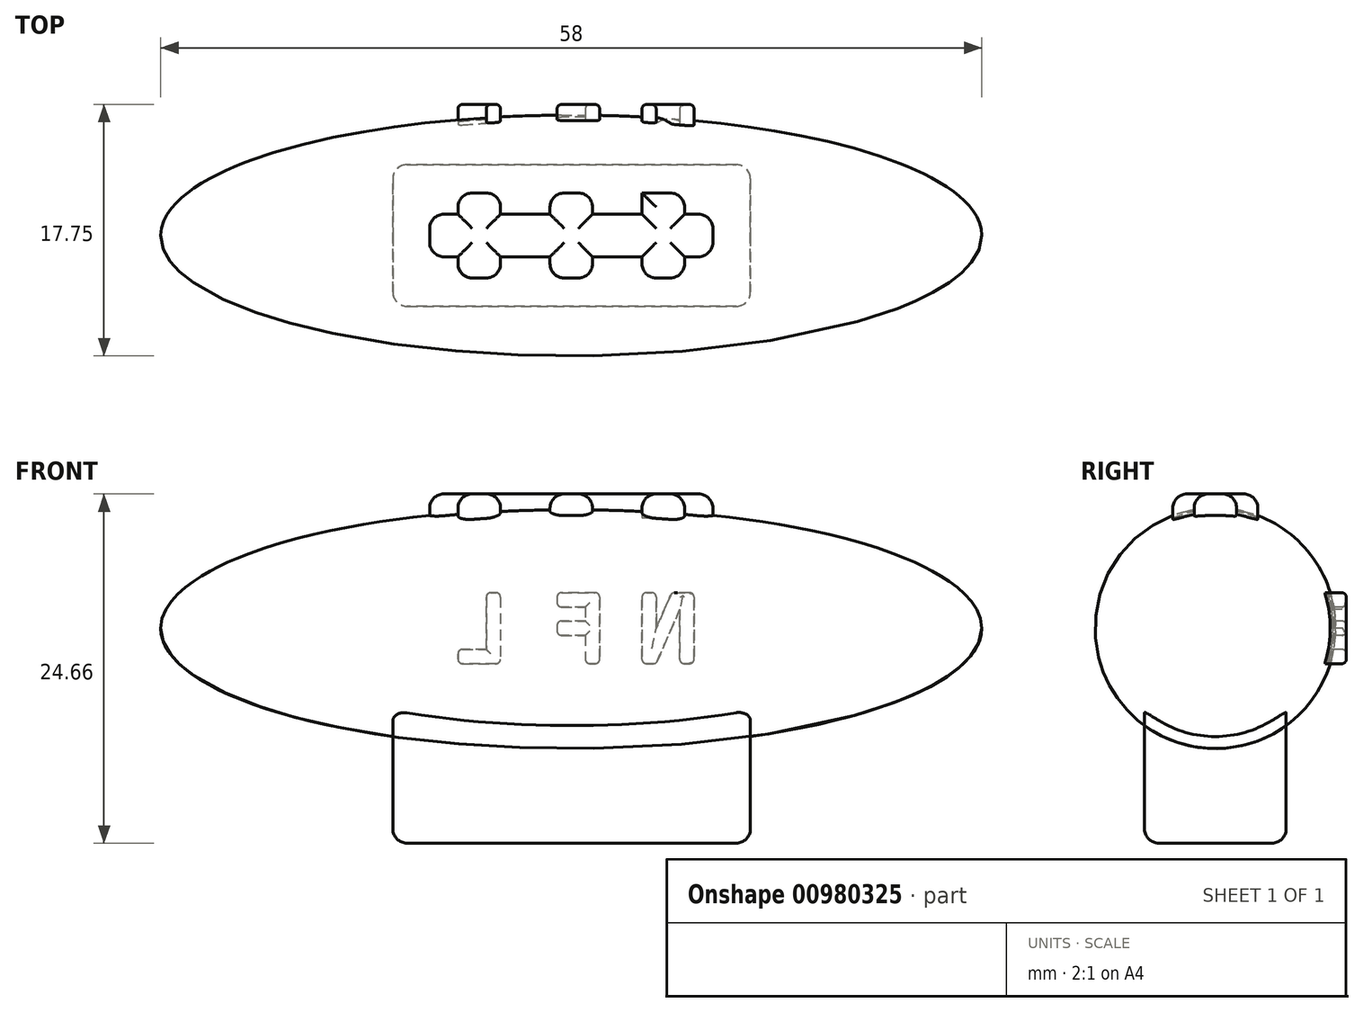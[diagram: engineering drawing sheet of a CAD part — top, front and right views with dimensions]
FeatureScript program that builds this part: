
annotation { "Feature Type Name" : "Feature", "Feature Type Description" : "" }
export const myFeature = defineFeature(function(context is Context, id is Id, definition is map)
    precondition{}
    {
        {
            var Q0;
            Q0=qCreatedBy(makeId("Front.planeOp"),FACE);
            var sketch = newSketch(context, id + "F0", { "sketchPlane" : qUnion([Q0])});
            skEllipse(sketch, "E0", {"center": v(0, 0) * mm, "majorRadius": 29 * mm, "minorRadius": 8.5 * mm, "majorAxis": v(-1, 0)});
            skLineSegment(sketch, "E1", {"start": v(-35.24, 0) * mm, "end": v(46.74, 0) * mm});
            skSolve(sketch);
        }
        {
            var Q0;
            {var subQ0=sQuery(id+"F0.wireOp",EDGE,"E1");var subQ1=sQuery(id+"F0.wireOp",EDGE,"E0");var subQ2=makeQuery(id+"F0.imprint","INTERSECT",VERTEX,{"disambiguationData":[OD(0.0)],"derivedFrom":[subQ1,subQ0]});Q0=makeQuery(id+"F0.imprint","IMPRINT",FACE,{"disambiguationData":[TD([[makeQuery(id+"F0.imprint","IMPRINT",EDGE,{"disambiguationData":[TD([[subQ2,1.0]])],"derivedFrom":subQ1}),1.0]])]});}
            var Q1;
            Q1=sQuery(id+"F0.wireOp",EDGE,"E1");
            revolve(context, id + "F1", {"surfaceOperationType" : NewSurfaceOperationType.NEW, "entities" : qUnion([Q0]), "axis" : qUnion([Q1]), "revolveType" : RevolveType.FULL});
        }
        {
            var Q0;
            Q0=qCreatedBy(makeId("Front.planeOp"),FACE);
            var sketch = newSketch(context, id + "F2", { "sketchPlane" : qUnion([Q0])});
            skLineSegment(sketch, "E2", {"start": v(-10, 7.5) * mm, "end": v(-10, 9.48) * mm});
            skLineSegment(sketch, "E3", {"start": v(-10, 9.48) * mm, "end": v(10, 9.48) * mm});
            skLineSegment(sketch, "E4", {"start": v(10, 9.48) * mm, "end": v(10, 7.5) * mm});
            skLineSegment(sketch, "E5", {"start": v(-10, 7.5) * mm, "end": v(10, 7.5) * mm});
            skSolve(sketch);
        }
        {
            var Q0;
            Q0 = qSketchRegion(id + "F2", true);
            extrude(context, id + "F3", {"entities" : qUnion([Q0]), "operationType" : NewBodyOperationType.ADD, "depth" : 3 * mm, "offsetDistance" : 25 * mm, "symmetric" : true});
        }
        {
            var Q0;
            Q0=qCreatedBy(makeId("Front.planeOp"),FACE);
            var sketch = newSketch(context, id + "F4", { "sketchPlane" : qUnion([Q0])});
            skLineSegment(sketch, "E6", {"start": v(-8, 9.48) * mm, "end": v(-8, 7.35) * mm});
            skLineSegment(sketch, "E7", {"start": v(-8, 7.35) * mm, "end": v(-5, 7.35) * mm});
            skLineSegment(sketch, "E8", {"start": v(-5, 7.35) * mm, "end": v(-5, 9.48) * mm});
            skLineSegment(sketch, "E9", {"start": v(-5, 9.48) * mm, "end": v(-8, 9.48) * mm});
            skLineSegment(sketch, "E10", {"start": v(-1.5, 9.48) * mm, "end": v(-1.5, 7.25) * mm});
            skLineSegment(sketch, "E11", {"start": v(-1.5, 7.25) * mm, "end": v(1.5, 7.25) * mm});
            skLineSegment(sketch, "E12", {"start": v(1.5, 7.25) * mm, "end": v(1.5, 9.48) * mm});
            skLineSegment(sketch, "E13", {"start": v(1.5, 9.48) * mm, "end": v(-1.5, 9.48) * mm});
            skLineSegment(sketch, "E14", {"start": v(5, 9.48) * mm, "end": v(5, 7.11) * mm});
            skLineSegment(sketch, "E15", {"start": v(5, 7.11) * mm, "end": v(8, 7.11) * mm});
            skLineSegment(sketch, "E16", {"start": v(8, 7.11) * mm, "end": v(8, 9.48) * mm});
            skLineSegment(sketch, "E17", {"start": v(8, 9.48) * mm, "end": v(5, 9.48) * mm});
            skSolve(sketch);
        }
        {
            var Q0;
            Q0=makeQuery(id+"F4.imprint","IMPRINT",FACE,{"disambiguationData":[TD([[makeQuery(id+"F4.imprint","IMPRINT",EDGE,{"derivedFrom":sQuery(id+"F4.wireOp",EDGE,"E6")}),1.0]])]});
            var Q1;
            Q1=makeQuery(id+"F4.imprint","IMPRINT",FACE,{"disambiguationData":[TD([[makeQuery(id+"F4.imprint","IMPRINT",EDGE,{"derivedFrom":sQuery(id+"F4.wireOp",EDGE,"E10")}),1.0]])]});
            var Q2;
            Q2=makeQuery(id+"F4.imprint","IMPRINT",FACE,{"disambiguationData":[TD([[makeQuery(id+"F4.imprint","IMPRINT",EDGE,{"derivedFrom":sQuery(id+"F4.wireOp",EDGE,"E14")}),1.0]])]});
            extrude(context, id + "F5", {"entities" : qUnion([Q0, Q1, Q2]), "operationType" : NewBodyOperationType.ADD, "depth" : 6 * mm, "offsetDistance" : 25 * mm, "symmetric" : true});
        }
        {
            var Q0;
            Q0=qCreatedBy(makeId("Front.planeOp"),FACE);
            var sketch = newSketch(context, id + "F6", { "sketchPlane" : qUnion([Q0])});
            skLineSegment(sketch, "E18", {"start": v(12.65, -5.45) * mm, "end": v(-12.6, -5.45) * mm});
            skLineSegment(sketch, "E19", {"start": v(-12.6, -5.45) * mm, "end": v(-12.6, -15.18) * mm});
            skLineSegment(sketch, "E20", {"start": v(-12.6, -15.18) * mm, "end": v(12.65, -15.18) * mm});
            skLineSegment(sketch, "E21", {"start": v(12.65, -5.45) * mm, "end": v(12.65, -15.18) * mm});
            skSolve(sketch);
        }
        {
            var Q0;
            Q0=makeQuery(id+"F6.imprint","IMPRINT",FACE,{"disambiguationData":[TD([[makeQuery(id+"F6.imprint","IMPRINT",EDGE,{"derivedFrom":sQuery(id+"F6.wireOp",EDGE,"E18")}),1.0]])]});
            extrude(context, id + "F7", {"entities" : qUnion([Q0]), "operationType" : NewBodyOperationType.ADD, "depth" : 10 * mm, "offsetDistance" : 25 * mm, "symmetric" : true});
        }
        {
            var Q0;
            Q0=qCreatedBy(makeId("Front.planeOp"),FACE);
            cPlane(context, id + "F8", {"entities" : qUnion([Q0]), "cplaneType" : CPlaneType.OFFSET, "offset" : 8.5 * mm, "oppositeDirection" : true, "width" : 150 * mm, "height" : 150 * mm});
        }
        {
            var Q0;
            Q0=qCreatedBy(id+"F8.planeOp",FACE);
            var sketch = newSketch(context, id + "F9", { "sketchPlane" : qUnion([Q0])});
            skLineSegment(sketch, "E22", {"start": v(8.67, -2.5) * mm, "end": v(8.67, 2.5) * mm});
            skLineSegment(sketch, "E23", {"start": v(8.67, 2.5) * mm, "end": v(7.1, 2.5) * mm});
            skLineSegment(sketch, "E24", {"start": v(7.1, 2.5) * mm, "end": v(6, 0) * mm});
            skLineSegment(sketch, "E25", {"start": v(6, 0) * mm, "end": v(6, 2.5) * mm});
            skLineSegment(sketch, "E26", {"start": v(8.67, -2.5) * mm, "end": v(7.67, -2.5) * mm});
            skLineSegment(sketch, "E27", {"start": v(7.67, -2.5) * mm, "end": v(7.67, 1.33) * mm});
            skLineSegment(sketch, "E28", {"start": v(5, 2.5) * mm, "end": v(6, 2.5) * mm});
            skLineSegment(sketch, "E29", {"start": v(7.67, 1.33) * mm, "end": v(6, -2.5) * mm});
            skLineSegment(sketch, "E30", {"start": v(6, -2.5) * mm, "end": v(5, -2.5) * mm});
            skLineSegment(sketch, "E31", {"start": v(5, -2.5) * mm, "end": v(5, 2.5) * mm});
            skLineSegment(sketch, "E32", {"start": v(2, -2.5) * mm, "end": v(2, 2.5) * mm});
            skLineSegment(sketch, "E33", {"start": v(2, 2.5) * mm, "end": v(-1, 2.5) * mm});
            skLineSegment(sketch, "E34", {"start": v(-1, 2.5) * mm, "end": v(-1, 1.5) * mm});
            skLineSegment(sketch, "E35", {"start": v(-1, 1.5) * mm, "end": v(1, 1.5) * mm});
            skLineSegment(sketch, "E36", {"start": v(1, 1.5) * mm, "end": v(1, 0.5) * mm});
            skLineSegment(sketch, "E37", {"start": v(1, 0.5) * mm, "end": v(-1, 0.5) * mm});
            skLineSegment(sketch, "E38", {"start": v(-1, 0.5) * mm, "end": v(-1, -0.5) * mm});
            skLineSegment(sketch, "E39", {"start": v(-1, -0.5) * mm, "end": v(1, -0.5) * mm});
            skLineSegment(sketch, "E40", {"start": v(1, -0.5) * mm, "end": v(1, -2.5) * mm});
            skLineSegment(sketch, "E41", {"start": v(1, -2.5) * mm, "end": v(2, -2.5) * mm});
            skLineSegment(sketch, "E42", {"start": v(-5, 2.5) * mm, "end": v(-5, -2.5) * mm});
            skLineSegment(sketch, "E43", {"start": v(-5, -2.5) * mm, "end": v(-8, -2.5) * mm});
            skLineSegment(sketch, "E44", {"start": v(-8, -2.5) * mm, "end": v(-8, -1.5) * mm});
            skLineSegment(sketch, "E45", {"start": v(-8, -1.5) * mm, "end": v(-6, -1.5) * mm});
            skLineSegment(sketch, "E46", {"start": v(-6, -1.5) * mm, "end": v(-6, 2.5) * mm});
            skLineSegment(sketch, "E47", {"start": v(-6, 2.5) * mm, "end": v(-5, 2.5) * mm});
            skSolve(sketch);
        }
        {
            var Q0;
            Q0=makeQuery(id+"F9.imprint","IMPRINT",FACE,{"disambiguationData":[TD([[makeQuery(id+"F9.imprint","IMPRINT",EDGE,{"derivedFrom":sQuery(id+"F9.wireOp",EDGE,"E22")}),1.0]])]});
            var Q1;
            Q1=makeQuery(id+"F9.imprint","IMPRINT",FACE,{"disambiguationData":[TD([[makeQuery(id+"F9.imprint","IMPRINT",EDGE,{"derivedFrom":sQuery(id+"F9.wireOp",EDGE,"E32")}),1.0]])]});
            var Q2;
            Q2=makeQuery(id+"F9.imprint","IMPRINT",FACE,{"disambiguationData":[TD([[makeQuery(id+"F9.imprint","IMPRINT",EDGE,{"derivedFrom":sQuery(id+"F9.wireOp",EDGE,"E42")}),-1.0]])]});
            extrude(context, id + "F10", {"entities" : qUnion([Q0, Q1, Q2]), "operationType" : NewBodyOperationType.ADD, "oppositeDirection" : true, "depth" : 1.5 * mm, "offsetDistance" : 25 * mm, "symmetric" : true});
        }
        {
            var Q0;
            Q0=makeQuery(id+"F5.opExtrude","CAP_EDGE",EDGE,{"disambiguationData":[OSD([sQuery(id+"F4.wireOp",EDGE,"E17")])],"isStart":false});
            var Q1;
            {var subQ0=sQuery(id+"F4.wireOp",EDGE,"E16");var subQ1=sQuery(id+"F2.wireOp",EDGE,"E3");var subQ2=sQuery(id+"F4.wireOp",EDGE,"E17");Q1=makeQuery(id+"F5.boolean.opBoolean","SPLIT",EDGE,{"disambiguationData":[TD([makeQuery(id+"F3.opExtrude","CAP_FACE",FACE,{"disambiguationData":[OSD([sQuery(id+"F2.wireOp",EDGE,"E2"),subQ1,sQuery(id+"F2.wireOp",EDGE,"E4"),sQuery(id+"F2.wireOp",EDGE,"E5")])],"isStart":false})])],"derivedFrom":makeQuery(id+"F5.opExtrude","SWEPT_EDGE",EDGE,{"disambiguationData":[OSD([subQ0,subQ2])]})});}
            var Q2;
            {var subQ0=sQuery(id+"F2.wireOp",EDGE,"E4");var subQ1=sQuery(id+"F2.wireOp",EDGE,"E3");Q2=makeQuery(id+"F5.boolean.opBoolean","SPLIT",EDGE,{"disambiguationData":[TD([makeQuery(id+"F3.opExtrude","SWEPT_FACE",FACE,{"disambiguationData":[OSD([subQ0])]})])],"derivedFrom":makeQuery(id+"F3.opExtrude","CAP_EDGE",EDGE,{"disambiguationData":[OSD([subQ1])],"isStart":false})});}
            var Q3;
            Q3=makeQuery(id+"F3.opExtrude","SWEPT_EDGE",EDGE,{"disambiguationData":[OSD([sQuery(id+"F2.wireOp",EDGE,"E3"),sQuery(id+"F2.wireOp",EDGE,"E4")])]});
            var Q4;
            {var subQ0=sQuery(id+"F2.wireOp",EDGE,"E4");var subQ1=sQuery(id+"F2.wireOp",EDGE,"E3");Q4=makeQuery(id+"F5.boolean.opBoolean","SPLIT",EDGE,{"disambiguationData":[TD([makeQuery(id+"F3.opExtrude","SWEPT_FACE",FACE,{"disambiguationData":[OSD([subQ0])]})])],"derivedFrom":makeQuery(id+"F3.opExtrude","CAP_EDGE",EDGE,{"disambiguationData":[OSD([subQ1])],"isStart":true})});}
            var Q5;
            {var subQ0=sQuery(id+"F4.wireOp",EDGE,"E16");var subQ1=sQuery(id+"F2.wireOp",EDGE,"E3");var subQ2=sQuery(id+"F4.wireOp",EDGE,"E17");Q5=makeQuery(id+"F5.boolean.opBoolean","SPLIT",EDGE,{"disambiguationData":[TD([makeQuery(id+"F3.opExtrude","CAP_FACE",FACE,{"disambiguationData":[OSD([sQuery(id+"F2.wireOp",EDGE,"E2"),subQ1,sQuery(id+"F2.wireOp",EDGE,"E4"),sQuery(id+"F2.wireOp",EDGE,"E5")])],"isStart":true})])],"derivedFrom":makeQuery(id+"F5.opExtrude","SWEPT_EDGE",EDGE,{"disambiguationData":[OSD([subQ0,subQ2])]})});}
            var Q6;
            {var subQ0=sQuery(id+"F2.wireOp",EDGE,"E3");Q6=makeQuery(id+"F5.boolean.opBoolean","SPLIT",EDGE,{"disambiguationData":[TD([makeQuery(id+"F5.opExtrude","SWEPT_FACE",FACE,{"disambiguationData":[OSD([sQuery(id+"F4.wireOp",EDGE,"E12")])]})])],"derivedFrom":makeQuery(id+"F3.opExtrude","CAP_EDGE",EDGE,{"disambiguationData":[OSD([subQ0])],"isStart":true})});}
            var Q7;
            {var subQ0=sQuery(id+"F2.wireOp",EDGE,"E3");var subQ1=sQuery(id+"F4.wireOp",EDGE,"E14");var subQ2=sQuery(id+"F4.wireOp",EDGE,"E17");Q7=makeQuery(id+"F5.boolean.opBoolean","SPLIT",EDGE,{"disambiguationData":[TD([makeQuery(id+"F3.opExtrude","CAP_FACE",FACE,{"disambiguationData":[OSD([sQuery(id+"F2.wireOp",EDGE,"E2"),subQ0,sQuery(id+"F2.wireOp",EDGE,"E4"),sQuery(id+"F2.wireOp",EDGE,"E5")])],"isStart":false})])],"derivedFrom":makeQuery(id+"F5.opExtrude","SWEPT_EDGE",EDGE,{"disambiguationData":[OSD([subQ1,subQ2])]})});}
            var Q8;
            Q8=makeQuery(id+"F5.opExtrude","CAP_EDGE",EDGE,{"disambiguationData":[OSD([sQuery(id+"F4.wireOp",EDGE,"E17")])],"isStart":true});
            var Q9;
            {var subQ0=sQuery(id+"F2.wireOp",EDGE,"E3");var subQ1=sQuery(id+"F4.wireOp",EDGE,"E14");var subQ2=sQuery(id+"F4.wireOp",EDGE,"E17");Q9=makeQuery(id+"F5.boolean.opBoolean","SPLIT",EDGE,{"disambiguationData":[TD([makeQuery(id+"F3.opExtrude","CAP_FACE",FACE,{"disambiguationData":[OSD([sQuery(id+"F2.wireOp",EDGE,"E2"),subQ0,sQuery(id+"F2.wireOp",EDGE,"E4"),sQuery(id+"F2.wireOp",EDGE,"E5")])],"isStart":true})])],"derivedFrom":makeQuery(id+"F5.opExtrude","SWEPT_EDGE",EDGE,{"disambiguationData":[OSD([subQ1,subQ2])]})});}
            var Q10;
            {var subQ0=sQuery(id+"F2.wireOp",EDGE,"E3");Q10=makeQuery(id+"F5.boolean.opBoolean","SPLIT",EDGE,{"disambiguationData":[TD([makeQuery(id+"F5.opExtrude","SWEPT_FACE",FACE,{"disambiguationData":[OSD([sQuery(id+"F4.wireOp",EDGE,"E12")])]})])],"derivedFrom":makeQuery(id+"F3.opExtrude","CAP_EDGE",EDGE,{"disambiguationData":[OSD([subQ0])],"isStart":false})});}
            var Q11;
            {var subQ0=sQuery(id+"F2.wireOp",EDGE,"E3");var subQ1=sQuery(id+"F4.wireOp",EDGE,"E13");var subQ2=sQuery(id+"F4.wireOp",EDGE,"E12");Q11=makeQuery(id+"F5.boolean.opBoolean","SPLIT",EDGE,{"disambiguationData":[TD([makeQuery(id+"F3.opExtrude","CAP_FACE",FACE,{"disambiguationData":[OSD([sQuery(id+"F2.wireOp",EDGE,"E2"),subQ0,sQuery(id+"F2.wireOp",EDGE,"E4"),sQuery(id+"F2.wireOp",EDGE,"E5")])],"isStart":false})])],"derivedFrom":makeQuery(id+"F5.opExtrude","SWEPT_EDGE",EDGE,{"disambiguationData":[OSD([subQ2,subQ1])]})});}
            var Q12;
            Q12=makeQuery(id+"F5.opExtrude","CAP_EDGE",EDGE,{"disambiguationData":[OSD([sQuery(id+"F4.wireOp",EDGE,"E13")])],"isStart":false});
            var Q13;
            {var subQ0=sQuery(id+"F4.wireOp",EDGE,"E10");var subQ1=sQuery(id+"F2.wireOp",EDGE,"E3");var subQ2=sQuery(id+"F4.wireOp",EDGE,"E13");Q13=makeQuery(id+"F5.boolean.opBoolean","SPLIT",EDGE,{"disambiguationData":[TD([makeQuery(id+"F3.opExtrude","CAP_FACE",FACE,{"disambiguationData":[OSD([sQuery(id+"F2.wireOp",EDGE,"E2"),subQ1,sQuery(id+"F2.wireOp",EDGE,"E4"),sQuery(id+"F2.wireOp",EDGE,"E5")])],"isStart":false})])],"derivedFrom":makeQuery(id+"F5.opExtrude","SWEPT_EDGE",EDGE,{"disambiguationData":[OSD([subQ0,subQ2])]})});}
            var Q14;
            {var subQ0=sQuery(id+"F2.wireOp",EDGE,"E3");Q14=makeQuery(id+"F5.boolean.opBoolean","SPLIT",EDGE,{"disambiguationData":[TD([makeQuery(id+"F5.opExtrude","SWEPT_FACE",FACE,{"disambiguationData":[OSD([sQuery(id+"F4.wireOp",EDGE,"E8")])]})])],"derivedFrom":makeQuery(id+"F3.opExtrude","CAP_EDGE",EDGE,{"disambiguationData":[OSD([subQ0])],"isStart":false})});}
            var Q15;
            {var subQ0=sQuery(id+"F4.wireOp",EDGE,"E9");var subQ1=sQuery(id+"F4.wireOp",EDGE,"E8");var subQ2=sQuery(id+"F2.wireOp",EDGE,"E3");Q15=makeQuery(id+"F5.boolean.opBoolean","SPLIT",EDGE,{"disambiguationData":[TD([makeQuery(id+"F3.opExtrude","CAP_FACE",FACE,{"disambiguationData":[OSD([sQuery(id+"F2.wireOp",EDGE,"E2"),subQ2,sQuery(id+"F2.wireOp",EDGE,"E4"),sQuery(id+"F2.wireOp",EDGE,"E5")])],"isStart":false})])],"derivedFrom":makeQuery(id+"F5.opExtrude","SWEPT_EDGE",EDGE,{"disambiguationData":[OSD([subQ1,subQ0])]})});}
            var Q16;
            Q16=makeQuery(id+"F5.opExtrude","CAP_EDGE",EDGE,{"disambiguationData":[OSD([sQuery(id+"F4.wireOp",EDGE,"E9")])],"isStart":false});
            var Q17;
            {var subQ0=sQuery(id+"F4.wireOp",EDGE,"E9");var subQ1=sQuery(id+"F4.wireOp",EDGE,"E6");var subQ2=sQuery(id+"F2.wireOp",EDGE,"E3");Q17=makeQuery(id+"F5.boolean.opBoolean","SPLIT",EDGE,{"disambiguationData":[TD([makeQuery(id+"F3.opExtrude","CAP_FACE",FACE,{"disambiguationData":[OSD([sQuery(id+"F2.wireOp",EDGE,"E2"),subQ2,sQuery(id+"F2.wireOp",EDGE,"E4"),sQuery(id+"F2.wireOp",EDGE,"E5")])],"isStart":false})])],"derivedFrom":makeQuery(id+"F5.opExtrude","SWEPT_EDGE",EDGE,{"disambiguationData":[OSD([subQ1,subQ0])]})});}
            var Q18;
            {var subQ0=sQuery(id+"F2.wireOp",EDGE,"E3");var subQ1=sQuery(id+"F2.wireOp",EDGE,"E2");Q18=makeQuery(id+"F5.boolean.opBoolean","SPLIT",EDGE,{"disambiguationData":[TD([makeQuery(id+"F3.opExtrude","SWEPT_FACE",FACE,{"disambiguationData":[OSD([subQ1])]})])],"derivedFrom":makeQuery(id+"F3.opExtrude","CAP_EDGE",EDGE,{"disambiguationData":[OSD([subQ0])],"isStart":false})});}
            var Q19;
            Q19=makeQuery(id+"F3.opExtrude","SWEPT_EDGE",EDGE,{"disambiguationData":[OSD([sQuery(id+"F2.wireOp",EDGE,"E2"),sQuery(id+"F2.wireOp",EDGE,"E3")])]});
            var Q20;
            {var subQ0=sQuery(id+"F2.wireOp",EDGE,"E3");var subQ1=sQuery(id+"F4.wireOp",EDGE,"E13");var subQ2=sQuery(id+"F4.wireOp",EDGE,"E12");Q20=makeQuery(id+"F5.boolean.opBoolean","SPLIT",EDGE,{"disambiguationData":[TD([makeQuery(id+"F3.opExtrude","CAP_FACE",FACE,{"disambiguationData":[OSD([sQuery(id+"F2.wireOp",EDGE,"E2"),subQ0,sQuery(id+"F2.wireOp",EDGE,"E4"),sQuery(id+"F2.wireOp",EDGE,"E5")])],"isStart":true})])],"derivedFrom":makeQuery(id+"F5.opExtrude","SWEPT_EDGE",EDGE,{"disambiguationData":[OSD([subQ2,subQ1])]})});}
            var Q21;
            Q21=makeQuery(id+"F5.opExtrude","CAP_EDGE",EDGE,{"disambiguationData":[OSD([sQuery(id+"F4.wireOp",EDGE,"E9")])],"isStart":true});
            var Q22;
            {var subQ0=sQuery(id+"F2.wireOp",EDGE,"E3");Q22=makeQuery(id+"F5.boolean.opBoolean","SPLIT",EDGE,{"disambiguationData":[TD([makeQuery(id+"F5.opExtrude","SWEPT_FACE",FACE,{"disambiguationData":[OSD([sQuery(id+"F4.wireOp",EDGE,"E8")])]})])],"derivedFrom":makeQuery(id+"F3.opExtrude","CAP_EDGE",EDGE,{"disambiguationData":[OSD([subQ0])],"isStart":true})});}
            var Q23;
            Q23=makeQuery(id+"F5.opExtrude","CAP_EDGE",EDGE,{"disambiguationData":[OSD([sQuery(id+"F4.wireOp",EDGE,"E13")])],"isStart":true});
            var Q24;
            {var subQ0=sQuery(id+"F4.wireOp",EDGE,"E10");var subQ1=sQuery(id+"F2.wireOp",EDGE,"E3");var subQ2=sQuery(id+"F4.wireOp",EDGE,"E13");Q24=makeQuery(id+"F5.boolean.opBoolean","SPLIT",EDGE,{"disambiguationData":[TD([makeQuery(id+"F3.opExtrude","CAP_FACE",FACE,{"disambiguationData":[OSD([sQuery(id+"F2.wireOp",EDGE,"E2"),subQ1,sQuery(id+"F2.wireOp",EDGE,"E4"),sQuery(id+"F2.wireOp",EDGE,"E5")])],"isStart":true})])],"derivedFrom":makeQuery(id+"F5.opExtrude","SWEPT_EDGE",EDGE,{"disambiguationData":[OSD([subQ0,subQ2])]})});}
            var Q25;
            {var subQ0=sQuery(id+"F4.wireOp",EDGE,"E9");var subQ1=sQuery(id+"F4.wireOp",EDGE,"E8");var subQ2=sQuery(id+"F2.wireOp",EDGE,"E3");Q25=makeQuery(id+"F5.boolean.opBoolean","SPLIT",EDGE,{"disambiguationData":[TD([makeQuery(id+"F3.opExtrude","CAP_FACE",FACE,{"disambiguationData":[OSD([sQuery(id+"F2.wireOp",EDGE,"E2"),subQ2,sQuery(id+"F2.wireOp",EDGE,"E4"),sQuery(id+"F2.wireOp",EDGE,"E5")])],"isStart":true})])],"derivedFrom":makeQuery(id+"F5.opExtrude","SWEPT_EDGE",EDGE,{"disambiguationData":[OSD([subQ1,subQ0])]})});}
            var Q26;
            {var subQ0=sQuery(id+"F4.wireOp",EDGE,"E9");var subQ1=sQuery(id+"F4.wireOp",EDGE,"E6");var subQ2=sQuery(id+"F2.wireOp",EDGE,"E3");Q26=makeQuery(id+"F5.boolean.opBoolean","SPLIT",EDGE,{"disambiguationData":[TD([makeQuery(id+"F3.opExtrude","CAP_FACE",FACE,{"disambiguationData":[OSD([sQuery(id+"F2.wireOp",EDGE,"E2"),subQ2,sQuery(id+"F2.wireOp",EDGE,"E4"),sQuery(id+"F2.wireOp",EDGE,"E5")])],"isStart":true})])],"derivedFrom":makeQuery(id+"F5.opExtrude","SWEPT_EDGE",EDGE,{"disambiguationData":[OSD([subQ1,subQ0])]})});}
            var Q27;
            {var subQ0=sQuery(id+"F2.wireOp",EDGE,"E3");var subQ1=sQuery(id+"F2.wireOp",EDGE,"E2");Q27=makeQuery(id+"F5.boolean.opBoolean","SPLIT",EDGE,{"disambiguationData":[TD([makeQuery(id+"F3.opExtrude","SWEPT_FACE",FACE,{"disambiguationData":[OSD([subQ1])]})])],"derivedFrom":makeQuery(id+"F3.opExtrude","CAP_EDGE",EDGE,{"disambiguationData":[OSD([subQ0])],"isStart":true})});}
            var Q28;
            Q28=makeQuery(id+"F5.opExtrude","CAP_EDGE",EDGE,{"disambiguationData":[OSD([sQuery(id+"F4.wireOp",EDGE,"E16")])],"isStart":true});
            var Q29;
            Q29=makeQuery(id+"F3.opExtrude","CAP_EDGE",EDGE,{"disambiguationData":[OSD([sQuery(id+"F2.wireOp",EDGE,"E4")])],"isStart":true});
            var Q30;
            Q30=makeQuery(id+"F3.opExtrude","CAP_EDGE",EDGE,{"disambiguationData":[OSD([sQuery(id+"F2.wireOp",EDGE,"E4")])],"isStart":false});
            var Q31;
            Q31=makeQuery(id+"F5.opExtrude","CAP_EDGE",EDGE,{"disambiguationData":[OSD([sQuery(id+"F4.wireOp",EDGE,"E12")])],"isStart":true});
            var Q32;
            Q32=makeQuery(id+"F5.opExtrude","CAP_EDGE",EDGE,{"disambiguationData":[OSD([sQuery(id+"F4.wireOp",EDGE,"E10")])],"isStart":true});
            var Q33;
            Q33=makeQuery(id+"F5.opExtrude","CAP_EDGE",EDGE,{"disambiguationData":[OSD([sQuery(id+"F4.wireOp",EDGE,"E8")])],"isStart":true});
            var Q34;
            Q34=makeQuery(id+"F5.opExtrude","CAP_EDGE",EDGE,{"disambiguationData":[OSD([sQuery(id+"F4.wireOp",EDGE,"E6")])],"isStart":true});
            var Q35;
            Q35=makeQuery(id+"F3.opExtrude","CAP_EDGE",EDGE,{"disambiguationData":[OSD([sQuery(id+"F2.wireOp",EDGE,"E2")])],"isStart":true});
            var Q36;
            Q36=makeQuery(id+"F3.opExtrude","CAP_EDGE",EDGE,{"disambiguationData":[OSD([sQuery(id+"F2.wireOp",EDGE,"E2")])],"isStart":false});
            var Q37;
            Q37=makeQuery(id+"F5.opExtrude","CAP_EDGE",EDGE,{"disambiguationData":[OSD([sQuery(id+"F4.wireOp",EDGE,"E6")])],"isStart":false});
            var Q38;
            Q38=makeQuery(id+"F5.opExtrude","CAP_EDGE",EDGE,{"disambiguationData":[OSD([sQuery(id+"F4.wireOp",EDGE,"E8")])],"isStart":false});
            var Q39;
            Q39=makeQuery(id+"F5.opExtrude","CAP_EDGE",EDGE,{"disambiguationData":[OSD([sQuery(id+"F4.wireOp",EDGE,"E10")])],"isStart":false});
            var Q40;
            Q40=makeQuery(id+"F5.opExtrude","CAP_EDGE",EDGE,{"disambiguationData":[OSD([sQuery(id+"F4.wireOp",EDGE,"E12")])],"isStart":false});
            var Q41;
            Q41=makeQuery(id+"F5.opExtrude","CAP_EDGE",EDGE,{"disambiguationData":[OSD([sQuery(id+"F4.wireOp",EDGE,"E14")])],"isStart":false});
            var Q42;
            Q42=makeQuery(id+"F5.opExtrude","CAP_EDGE",EDGE,{"disambiguationData":[OSD([sQuery(id+"F4.wireOp",EDGE,"E16")])],"isStart":false});
            fillet(context, id + "F11", {"entities" : qUnion([Q0, Q1, Q2, Q3, Q4, Q5, Q6, Q7, Q8, Q9, Q10, Q11, Q12, Q13, Q14, Q15, Q16, Q17, Q18, Q19, Q20, Q21, Q22, Q23, Q24, Q25, Q26, Q27, Q28, Q29, Q30, Q31, Q32, Q33, Q34, Q35, Q36, Q37, Q38, Q39, Q40, Q41, Q42]), "radius" : 1 * mm, "tangentPropagation" : true, "allowEdgeOverflow" : false});
        }
        {
            var Q0;
            Q0=makeQuery(id+"F10.opExtrude","CAP_EDGE",EDGE,{"disambiguationData":[OSD([sQuery(id+"F9.wireOp",EDGE,"E23")])],"isStart":false});
            var Q1;
            Q1=makeQuery(id+"F10.opExtrude","CAP_EDGE",EDGE,{"disambiguationData":[OSD([sQuery(id+"F9.wireOp",EDGE,"E22")])],"isStart":false});
            var Q2;
            Q2=makeQuery(id+"F10.opExtrude","CAP_EDGE",EDGE,{"disambiguationData":[OSD([sQuery(id+"F9.wireOp",EDGE,"E29")])],"isStart":false});
            var Q3;
            Q3=makeQuery(id+"F10.opExtrude","CAP_EDGE",EDGE,{"disambiguationData":[OSD([sQuery(id+"F9.wireOp",EDGE,"E27")])],"isStart":false});
            var Q4;
            Q4=makeQuery(id+"F10.opExtrude","CAP_EDGE",EDGE,{"disambiguationData":[OSD([sQuery(id+"F9.wireOp",EDGE,"E26")])],"isStart":false});
            var Q5;
            Q5=makeQuery(id+"F10.opExtrude","CAP_EDGE",EDGE,{"disambiguationData":[OSD([sQuery(id+"F9.wireOp",EDGE,"E24")])],"isStart":false});
            var Q6;
            Q6=makeQuery(id+"F10.opExtrude","CAP_EDGE",EDGE,{"disambiguationData":[OSD([sQuery(id+"F9.wireOp",EDGE,"E25")])],"isStart":false});
            var Q7;
            Q7=makeQuery(id+"F10.opExtrude","CAP_EDGE",EDGE,{"disambiguationData":[OSD([sQuery(id+"F9.wireOp",EDGE,"E28")])],"isStart":false});
            var Q8;
            Q8=makeQuery(id+"F10.opExtrude","CAP_EDGE",EDGE,{"disambiguationData":[OSD([sQuery(id+"F9.wireOp",EDGE,"E31")])],"isStart":false});
            var Q9;
            Q9=makeQuery(id+"F10.opExtrude","CAP_EDGE",EDGE,{"disambiguationData":[OSD([sQuery(id+"F9.wireOp",EDGE,"E30")])],"isStart":false});
            var Q10;
            Q10=makeQuery(id+"F10.opExtrude","SWEPT_EDGE",EDGE,{"disambiguationData":[OSD([sQuery(id+"F9.wireOp",EDGE,"E28"),sQuery(id+"F9.wireOp",EDGE,"E31")])]});
            var Q11;
            Q11=makeQuery(id+"F10.opExtrude","SWEPT_EDGE",EDGE,{"disambiguationData":[OSD([sQuery(id+"F9.wireOp",EDGE,"E25"),sQuery(id+"F9.wireOp",EDGE,"E28")])]});
            var Q12;
            Q12=makeQuery(id+"F10.opExtrude","SWEPT_EDGE",EDGE,{"disambiguationData":[OSD([sQuery(id+"F9.wireOp",EDGE,"E23"),sQuery(id+"F9.wireOp",EDGE,"E24")])]});
            var Q13;
            Q13=makeQuery(id+"F10.opExtrude","SWEPT_EDGE",EDGE,{"disambiguationData":[OSD([sQuery(id+"F9.wireOp",EDGE,"E22"),sQuery(id+"F9.wireOp",EDGE,"E23")])]});
            var Q14;
            Q14=makeQuery(id+"F10.opExtrude","SWEPT_EDGE",EDGE,{"disambiguationData":[OSD([sQuery(id+"F9.wireOp",EDGE,"E29"),sQuery(id+"F9.wireOp",EDGE,"E30")])]});
            var Q15;
            Q15=makeQuery(id+"F10.opExtrude","SWEPT_EDGE",EDGE,{"disambiguationData":[OSD([sQuery(id+"F9.wireOp",EDGE,"E22"),sQuery(id+"F9.wireOp",EDGE,"E26")])]});
            var Q16;
            Q16=makeQuery(id+"F10.opExtrude","SWEPT_EDGE",EDGE,{"disambiguationData":[OSD([sQuery(id+"F9.wireOp",EDGE,"E26"),sQuery(id+"F9.wireOp",EDGE,"E27")])]});
            var Q17;
            Q17=makeQuery(id+"F10.opExtrude","SWEPT_EDGE",EDGE,{"disambiguationData":[OSD([sQuery(id+"F9.wireOp",EDGE,"E30"),sQuery(id+"F9.wireOp",EDGE,"E31")])]});
            var Q18;
            Q18=makeQuery(id+"F10.opExtrude","CAP_EDGE",EDGE,{"disambiguationData":[OSD([sQuery(id+"F9.wireOp",EDGE,"E33")])],"isStart":false});
            var Q19;
            Q19=makeQuery(id+"F10.opExtrude","SWEPT_EDGE",EDGE,{"disambiguationData":[OSD([sQuery(id+"F9.wireOp",EDGE,"E32"),sQuery(id+"F9.wireOp",EDGE,"E33")])]});
            var Q20;
            Q20=makeQuery(id+"F10.opExtrude","CAP_EDGE",EDGE,{"disambiguationData":[OSD([sQuery(id+"F9.wireOp",EDGE,"E32")])],"isStart":false});
            var Q21;
            Q21=makeQuery(id+"F10.opExtrude","CAP_EDGE",EDGE,{"disambiguationData":[OSD([sQuery(id+"F9.wireOp",EDGE,"E36")])],"isStart":false});
            var Q22;
            Q22=makeQuery(id+"F10.opExtrude","CAP_EDGE",EDGE,{"disambiguationData":[OSD([sQuery(id+"F9.wireOp",EDGE,"E35")])],"isStart":false});
            var Q23;
            Q23=makeQuery(id+"F10.opExtrude","CAP_EDGE",EDGE,{"disambiguationData":[OSD([sQuery(id+"F9.wireOp",EDGE,"E37")])],"isStart":false});
            var Q24;
            Q24=makeQuery(id+"F10.opExtrude","CAP_EDGE",EDGE,{"disambiguationData":[OSD([sQuery(id+"F9.wireOp",EDGE,"E39")])],"isStart":false});
            var Q25;
            Q25=makeQuery(id+"F10.opExtrude","CAP_EDGE",EDGE,{"disambiguationData":[OSD([sQuery(id+"F9.wireOp",EDGE,"E38")])],"isStart":false});
            var Q26;
            Q26=makeQuery(id+"F10.opExtrude","CAP_EDGE",EDGE,{"disambiguationData":[OSD([sQuery(id+"F9.wireOp",EDGE,"E40")])],"isStart":false});
            var Q27;
            Q27=makeQuery(id+"F10.opExtrude","CAP_EDGE",EDGE,{"disambiguationData":[OSD([sQuery(id+"F9.wireOp",EDGE,"E41")])],"isStart":false});
            var Q28;
            Q28=makeQuery(id+"F10.opExtrude","CAP_EDGE",EDGE,{"disambiguationData":[OSD([sQuery(id+"F9.wireOp",EDGE,"E34")])],"isStart":false});
            var Q29;
            Q29=makeQuery(id+"F10.opExtrude","SWEPT_EDGE",EDGE,{"disambiguationData":[OSD([sQuery(id+"F9.wireOp",EDGE,"E33"),sQuery(id+"F9.wireOp",EDGE,"E34")])]});
            var Q30;
            Q30=makeQuery(id+"F10.opExtrude","SWEPT_EDGE",EDGE,{"disambiguationData":[OSD([sQuery(id+"F9.wireOp",EDGE,"E34"),sQuery(id+"F9.wireOp",EDGE,"E35")])]});
            var Q31;
            Q31=makeQuery(id+"F10.opExtrude","SWEPT_EDGE",EDGE,{"disambiguationData":[OSD([sQuery(id+"F9.wireOp",EDGE,"E37"),sQuery(id+"F9.wireOp",EDGE,"E38")])]});
            var Q32;
            Q32=makeQuery(id+"F10.opExtrude","SWEPT_EDGE",EDGE,{"disambiguationData":[OSD([sQuery(id+"F9.wireOp",EDGE,"E38"),sQuery(id+"F9.wireOp",EDGE,"E39")])]});
            var Q33;
            Q33=makeQuery(id+"F10.opExtrude","SWEPT_EDGE",EDGE,{"disambiguationData":[OSD([sQuery(id+"F9.wireOp",EDGE,"E40"),sQuery(id+"F9.wireOp",EDGE,"E41")])]});
            var Q34;
            Q34=makeQuery(id+"F10.opExtrude","SWEPT_EDGE",EDGE,{"disambiguationData":[OSD([sQuery(id+"F9.wireOp",EDGE,"E32"),sQuery(id+"F9.wireOp",EDGE,"E41")])]});
            var Q35;
            Q35=makeQuery(id+"F10.opExtrude","CAP_EDGE",EDGE,{"disambiguationData":[OSD([sQuery(id+"F9.wireOp",EDGE,"E45")])],"isStart":false});
            var Q36;
            Q36=makeQuery(id+"F10.opExtrude","CAP_EDGE",EDGE,{"disambiguationData":[OSD([sQuery(id+"F9.wireOp",EDGE,"E44")])],"isStart":false});
            var Q37;
            Q37=makeQuery(id+"F10.opExtrude","SWEPT_EDGE",EDGE,{"disambiguationData":[OSD([sQuery(id+"F9.wireOp",EDGE,"E43"),sQuery(id+"F9.wireOp",EDGE,"E44")])]});
            var Q38;
            Q38=makeQuery(id+"F10.opExtrude","SWEPT_EDGE",EDGE,{"disambiguationData":[OSD([sQuery(id+"F9.wireOp",EDGE,"E44"),sQuery(id+"F9.wireOp",EDGE,"E45")])]});
            var Q39;
            Q39=makeQuery(id+"F10.opExtrude","CAP_EDGE",EDGE,{"disambiguationData":[OSD([sQuery(id+"F9.wireOp",EDGE,"E43")])],"isStart":false});
            var Q40;
            Q40=makeQuery(id+"F10.opExtrude","SWEPT_EDGE",EDGE,{"disambiguationData":[OSD([sQuery(id+"F9.wireOp",EDGE,"E42"),sQuery(id+"F9.wireOp",EDGE,"E43")])]});
            var Q41;
            Q41=makeQuery(id+"F10.opExtrude","CAP_EDGE",EDGE,{"disambiguationData":[OSD([sQuery(id+"F9.wireOp",EDGE,"E42")])],"isStart":false});
            var Q42;
            Q42=makeQuery(id+"F10.opExtrude","CAP_EDGE",EDGE,{"disambiguationData":[OSD([sQuery(id+"F9.wireOp",EDGE,"E46")])],"isStart":false});
            var Q43;
            Q43=makeQuery(id+"F10.opExtrude","SWEPT_EDGE",EDGE,{"disambiguationData":[OSD([sQuery(id+"F9.wireOp",EDGE,"E46"),sQuery(id+"F9.wireOp",EDGE,"E47")])]});
            var Q44;
            Q44=makeQuery(id+"F10.opExtrude","SWEPT_EDGE",EDGE,{"disambiguationData":[OSD([sQuery(id+"F9.wireOp",EDGE,"E42"),sQuery(id+"F9.wireOp",EDGE,"E47")])]});
            var Q45;
            Q45=makeQuery(id+"F10.opExtrude","CAP_EDGE",EDGE,{"disambiguationData":[OSD([sQuery(id+"F9.wireOp",EDGE,"E47")])],"isStart":false});
            fillet(context, id + "F12", {"entities" : qUnion([Q0, Q1, Q2, Q3, Q4, Q5, Q6, Q7, Q8, Q9, Q10, Q11, Q12, Q13, Q14, Q15, Q16, Q17, Q18, Q19, Q20, Q21, Q22, Q23, Q24, Q25, Q26, Q27, Q28, Q29, Q30, Q31, Q32, Q33, Q34, Q35, Q36, Q37, Q38, Q39, Q40, Q41, Q42, Q43, Q44, Q45]), "radius" : 0.3 * mm, "tangentPropagation" : true, "allowEdgeOverflow" : false});
        }
        {
            var Q0;
            Q0=makeQuery(id+"F7.opExtrude","CAP_EDGE",EDGE,{"disambiguationData":[OSD([sQuery(id+"F6.wireOp",EDGE,"E21")])],"isStart":true});
            var Q1;
            Q1=makeQuery(id+"F7.opExtrude","CAP_EDGE",EDGE,{"disambiguationData":[OSD([sQuery(id+"F6.wireOp",EDGE,"E20")])],"isStart":true});
            var Q2;
            Q2=makeQuery(id+"F7.opExtrude","CAP_EDGE",EDGE,{"disambiguationData":[OSD([sQuery(id+"F6.wireOp",EDGE,"E19")])],"isStart":true});
            var Q3;
            Q3=makeQuery(id+"F7.opExtrude","SWEPT_EDGE",EDGE,{"disambiguationData":[OSD([sQuery(id+"F6.wireOp",EDGE,"E19"),sQuery(id+"F6.wireOp",EDGE,"E20")])]});
            var Q4;
            Q4=makeQuery(id+"F7.opExtrude","CAP_EDGE",EDGE,{"disambiguationData":[OSD([sQuery(id+"F6.wireOp",EDGE,"E19")])],"isStart":false});
            var Q5;
            Q5=makeQuery(id+"F7.opExtrude","CAP_EDGE",EDGE,{"disambiguationData":[OSD([sQuery(id+"F6.wireOp",EDGE,"E20")])],"isStart":false});
            var Q6;
            Q6=makeQuery(id+"F7.opExtrude","SWEPT_EDGE",EDGE,{"disambiguationData":[OSD([sQuery(id+"F6.wireOp",EDGE,"E20"),sQuery(id+"F6.wireOp",EDGE,"E21")])]});
            var Q7;
            Q7=makeQuery(id+"F7.opExtrude","CAP_EDGE",EDGE,{"disambiguationData":[OSD([sQuery(id+"F6.wireOp",EDGE,"E21")])],"isStart":false});
            fillet(context, id + "F13", {"entities" : qUnion([Q0, Q1, Q2, Q3, Q4, Q5, Q6, Q7]), "radius" : 1 * mm, "tangentPropagation" : true, "allowEdgeOverflow" : false});
        }
    });
